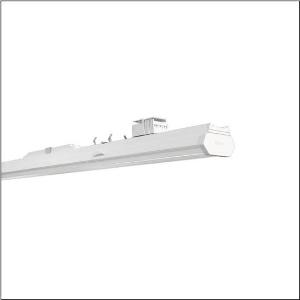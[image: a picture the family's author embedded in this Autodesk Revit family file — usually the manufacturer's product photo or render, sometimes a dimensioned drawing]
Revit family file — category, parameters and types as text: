
# Revit family: licross_r__21_protected_mo_52tp11cn49xg_f153
name_source: partatom
category: Lighting Fixtures
units: mm (PartAtom-declared; Revit-internal decimal feet)

## family parameters
Cut with Voids When Loaded = No
Host = Face
Light Source = No
Part Type = Normal
Room Calculation Point = No
Round Connector Dimension = Use Diameter
Shared = No

## types (1)
- --- (1 x LED, 9070 lm, 50.4 W, 4000K)
    Apparent Load = 50 VA
    CIE Flux Codes = 83 94 98 100 100
    Color Rendering = 80
    Color Temperature = 4000K
    Default Elevation = 1800 mm
    Description = Licross® 21 Protected MO, luminaire insert, of sheet steel, galvanised, coil coated, white, length: 1.500mm, width: 90mm, height: 103mm, LED rated luminous flux: 9.080lm, light colour: 840, SDCM (Standard Deviation of Colour Matching)MacAdam ≤ 3 SDCM (initial), control gear: ON/OFF Multilumen, CLOi, with plug, 3-pole, with phase selection, mains connection: 220..240V, AC, 50/60Hz, start of lifetime: 50W, end of service life: 61W, internal wiring halogen-free, primary light control with lens, of plastic, primary optical cover: cover, of PMMA, light emission: direct distribution, primary light characteristic: symmetric, protection rating (complete): IP64, insulation class (complete): insulation class I (protective earthing), certification: CE, ENEC, VDE, UKCA, protection symbol: D if used in an environment with conductive dust loads with corresponding accessories, impact resistance: IK06, permissible ambient temperature for indoor applications: -35..+45°C, corresponds to IFS (International Featured Standards) requirements for safety and quality in the food industry, reducing of maximum allowable ambient temperature of 5°C with ceiling mounting, LABS conformity tested according to VDMA 24364:2018-05, packaging unit: 1 piece
    Height = 92 mm
    Lamp = 1 x LED
    Lamp Light Flux = 9070 lm
    Lamp Power = 50.4 W
    Lamp count = 1
    Length = 1500 mm
    Luminous efficacy = 180 lm/W
    Manufacturer = Siteco
    ModVariant = No
    Model = 52TP11CN49XG
    Mounting Place = Ceiling
    Mounting Type = Pendant
    Number of Poles = 1
    OnlyDefault = Yes
    Power Factor = 1
    Product Name = Licross® 21 Protected MO
    Product group = luminaire insert | ceiling pendant
    ProductGroupID = 901
    Protection Class = Protection class I
    Protection Degree = IP 64
    RLX_Detail_Level = 1
    RLX_Emergency_Light_Flux = 0 lm
    RLX_Emergency_Type = 0
    RLX_Emergency_Type_DB = No
    RlxData = <blob elided: 21949 chars, md5=8d88d3d3>
    Socket = socket
    Standby Power = 0 W
    System Light Flux = 9070 lm
    System Power = 50 W
    Type Comments = factory setting: luminous flux: 100 % | (A | C | E) | 117 mA
    Type Image = l_1256148.jpg
    URL = http://relux.com
    VarID = @adj_114767
    Voltage = 0 V
    Weight = 0.00 kg
    Width = 88 mm

## geometry (parser evidence)
native form markers: Blend x4, Sweep x11
no freeform markers — native parametric forms only
